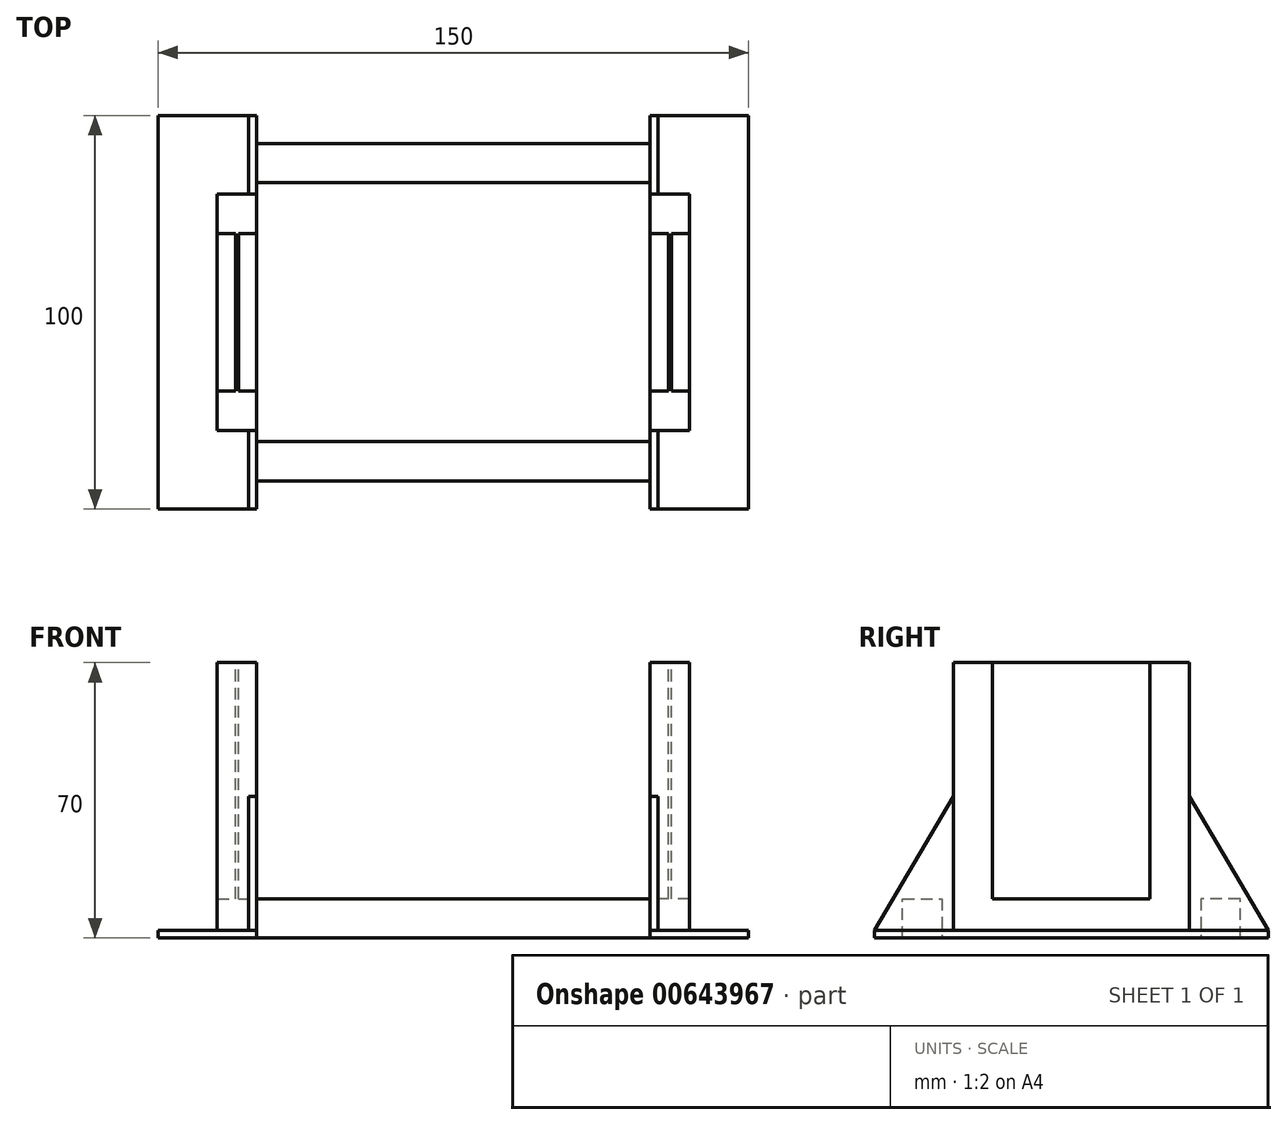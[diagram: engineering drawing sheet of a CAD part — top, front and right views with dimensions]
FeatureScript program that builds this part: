
annotation { "Feature Type Name" : "Feature", "Feature Type Description" : "" }
export const myFeature = defineFeature(function(context is Context, id is Id, definition is map)
    precondition{}
    {
        {
            var Q0;
            Q0=qCreatedBy(makeId("Right.planeOp"),FACE);
            var sketch = newSketch(context, id + "F0", { "sketchPlane" : qUnion([Q0])});
            skLineSegment(sketch, "E0", {"start": v(0, 0) * mm, "end": v(30, 0) * mm});
            skLineSegment(sketch, "E1", {"start": v(30, 0) * mm, "end": v(30, 70) * mm});
            skLineSegment(sketch, "E2", {"start": v(30, 70) * mm, "end": v(20, 70) * mm});
            skLineSegment(sketch, "E3", {"start": v(20, 70) * mm, "end": v(20, 10) * mm});
            skLineSegment(sketch, "E4", {"start": v(20, 10) * mm, "end": v(-20, 10) * mm});
            skLineSegment(sketch, "E5", {"start": v(-20, 10) * mm, "end": v(-20, 70) * mm});
            skLineSegment(sketch, "E6", {"start": v(-20, 70) * mm, "end": v(-30, 70) * mm});
            skLineSegment(sketch, "E7", {"start": v(-30, 70) * mm, "end": v(-30, 0) * mm});
            skLineSegment(sketch, "E8", {"start": v(-30, 0) * mm, "end": v(0, 0) * mm});
            skSolve(sketch);
        }
        {
            var Q0;
            Q0=makeQuery(id+"F0.imprint","IMPRINT",FACE,{"disambiguationData":[TD([[makeQuery(id+"F0.imprint","IMPRINT",EDGE,{"derivedFrom":sQuery(id+"F0.wireOp",EDGE,"E0")}),1.0]])]});
            extrude(context, id + "F1", {"entities" : qUnion([Q0]), "depth" : 10 * mm, "offsetDistance" : 25 * mm});
        }
        {
            var Q0;
            Q0=qCreatedBy(makeId("Right.planeOp"),FACE);
            cPlane(context, id + "F2", {"entities" : qUnion([Q0]), "cplaneType" : CPlaneType.OFFSET, "offset" : 5 * mm, "width" : 150 * mm, "height" : 150 * mm});
        }
        {
            var Q0;
            Q0=qCreatedBy(id+"F2.planeOp",FACE);
            var sketch = newSketch(context, id + "F3", { "sketchPlane" : qUnion([Q0])});
            skLineSegment(sketch, "E9", {"start": v(0, 0) * mm, "end": v(0, 10) * mm, "construction": true});
            skLineSegment(sketch, "E10", {"start": v(0, 10) * mm, "end": v(20, 10) * mm});
            skLineSegment(sketch, "E11", {"start": v(20, 10) * mm, "end": v(20, 70) * mm});
            skLineSegment(sketch, "E12", {"start": v(20, 70) * mm, "end": v(-20, 70) * mm});
            skLineSegment(sketch, "E13", {"start": v(-20, 70) * mm, "end": v(-20, 10) * mm});
            skLineSegment(sketch, "E14", {"start": v(-20, 10) * mm, "end": v(0, 10) * mm});
            skSolve(sketch);
        }
        {
            var Q0;
            Q0=makeQuery(id+"F3.imprint","IMPRINT",FACE,{"disambiguationData":[TD([[makeQuery(id+"F3.imprint","IMPRINT",EDGE,{"derivedFrom":sQuery(id+"F3.wireOp",EDGE,"E10")}),1.0]])]});
            extrude(context, id + "F4", {"entities" : qUnion([Q0]), "operationType" : NewBodyOperationType.ADD, "endBound" : BoundingType.SYMMETRIC, "depth" : .75 * mm, "offsetDistance" : 25 * mm});
        }
        {
            var Q0;
            Q0=makeQuery(id+"F1.opExtrude","CAP_FACE",FACE,{"disambiguationData":[OSD([sQuery(id+"F0.wireOp",EDGE,"E0"),sQuery(id+"F0.wireOp",EDGE,"E1"),sQuery(id+"F0.wireOp",EDGE,"E2"),sQuery(id+"F0.wireOp",EDGE,"E3"),sQuery(id+"F0.wireOp",EDGE,"E4"),sQuery(id+"F0.wireOp",EDGE,"E5"),sQuery(id+"F0.wireOp",EDGE,"E6"),sQuery(id+"F0.wireOp",EDGE,"E7"),sQuery(id+"F0.wireOp",EDGE,"E8")])],"isStart":true});
            var sketch = newSketch(context, id + "F5", { "sketchPlane" : qUnion([Q0])});
            skLineSegment(sketch, "E15", {"start": v(0, 0) * mm, "end": v(50, 0) * mm});
            skLineSegment(sketch, "E16", {"start": v(50, 0) * mm, "end": v(50, 2) * mm});
            skLineSegment(sketch, "E17", {"start": v(50, 2) * mm, "end": v(-50, 2) * mm});
            skLineSegment(sketch, "E18", {"start": v(-50, 2) * mm, "end": v(-50, 0) * mm});
            skLineSegment(sketch, "E19", {"start": v(-50, 0) * mm, "end": v(0, 0) * mm});
            skSolve(sketch);
        }
        {
            var Q0;
            {var subQ0=sQuery(id+"F5.wireOp",EDGE,"E17");var subQ1=makeQuery(id+"F1.opExtrude","CAP_EDGE",EDGE,{"disambiguationData":[OSD([sQuery(id+"F0.wireOp",EDGE,"E7")])],"isStart":true});var subQ2=makeQuery(id+"F5.imprint","INTERSECT",VERTEX,{"derivedFrom":[subQ1,subQ0]});Q0=makeQuery(id+"F5.imprint","IMPRINT",FACE,{"disambiguationData":[TD([[makeQuery(id+"F5.imprint","IMPRINT",EDGE,{"disambiguationData":[TD([[subQ2,-1.0]])],"derivedFrom":subQ0}),1.0]])]});}
            var Q1;
            {var subQ3=sQuery(id+"F5.wireOp",EDGE,"E16");Q1=makeQuery(id+"F5.imprint","IMPRINT",FACE,{"disambiguationData":[TD([[makeQuery(id+"F5.imprint","IMPRINT",EDGE,{"derivedFrom":subQ3}),1.0]])]});}
            var Q2;
            {var subQ0=sQuery(id+"F5.wireOp",EDGE,"E18");Q2=makeQuery(id+"F5.imprint","IMPRINT",FACE,{"disambiguationData":[TD([[makeQuery(id+"F5.imprint","IMPRINT",EDGE,{"derivedFrom":subQ0}),1.0]])]});}
            extrude(context, id + "F6", {"entities" : qUnion([Q0, Q1, Q2]), "operationType" : NewBodyOperationType.ADD, "oppositeDirection" : true, "depth" : 25 * mm, "offsetDistance" : 25 * mm});
        }
        {
            var Q0;
            Q0=makeQuery(id+"F6.boolean.opBoolean","MERGE",FACE,{"derivedFrom":[makeQuery(id+"F1.opExtrude","CAP_FACE",FACE,{"disambiguationData":[OSD([sQuery(id+"F0.wireOp",EDGE,"E0"),sQuery(id+"F0.wireOp",EDGE,"E1"),sQuery(id+"F0.wireOp",EDGE,"E2"),sQuery(id+"F0.wireOp",EDGE,"E3"),sQuery(id+"F0.wireOp",EDGE,"E4"),sQuery(id+"F0.wireOp",EDGE,"E5"),sQuery(id+"F0.wireOp",EDGE,"E6"),sQuery(id+"F0.wireOp",EDGE,"E7"),sQuery(id+"F0.wireOp",EDGE,"E8")])],"isStart":true}),makeQuery(id+"F6.opExtrude","CAP_FACE",FACE,{"disambiguationData":[OSD([sQuery(id+"F5.wireOp",EDGE,"E15"),sQuery(id+"F5.wireOp",EDGE,"E16"),sQuery(id+"F5.wireOp",EDGE,"E17"),sQuery(id+"F5.wireOp",EDGE,"E18"),sQuery(id+"F5.wireOp",EDGE,"E19")])],"isStart":true})]});
            var sketch = newSketch(context, id + "F7", { "sketchPlane" : qUnion([Q0])});
            skLineSegment(sketch, "E20", {"start": v(-30, 2) * mm, "end": v(-50, 2) * mm});
            skLineSegment(sketch, "E21", {"start": v(-50, 2) * mm, "end": v(-30, 36) * mm});
            skLineSegment(sketch, "E22", {"start": v(-30, 36) * mm, "end": v(-30, 2) * mm});
            skLineSegment(sketch, "E23.MirrorCS", {"start": v(50, 2) * mm, "end": v(30, 36) * mm});
            skLineSegment(sketch, "E24.MirrorCS", {"start": v(30, 2) * mm, "end": v(50, 2) * mm});
            skLineSegment(sketch, "E25.MirrorCS", {"start": v(30, 36) * mm, "end": v(30, 2) * mm});
            skSolve(sketch);
        }
        {
            var Q0;
            Q0=makeQuery(id+"F7.imprint","IMPRINT",FACE,{"disambiguationData":[TD([[makeQuery(id+"F7.imprint","IMPRINT",EDGE,{"derivedFrom":sQuery(id+"F7.wireOp",EDGE,"E20")}),-1.0]])]});
            var Q1;
            Q1=makeQuery(id+"F7.imprint","IMPRINT",FACE,{"disambiguationData":[TD([[makeQuery(id+"F7.imprint","IMPRINT",EDGE,{"derivedFrom":sQuery(id+"F7.wireOp",EDGE,"E23.MirrorCS")}),1.0]])]});
            extrude(context, id + "F8", {"entities" : qUnion([Q0, Q1]), "operationType" : NewBodyOperationType.ADD, "oppositeDirection" : true, "depth" : 2 * mm, "offsetDistance" : 25 * mm});
        }
        {
            var Q0;
            Q0=makeQuery(id+"F8.boolean.opBoolean","MERGE",FACE,{"derivedFrom":[makeQuery(id+"F6.boolean.opBoolean","MERGE",FACE,{"derivedFrom":[makeQuery(id+"F1.opExtrude","CAP_FACE",FACE,{"disambiguationData":[OSD([sQuery(id+"F0.wireOp",EDGE,"E0"),sQuery(id+"F0.wireOp",EDGE,"E1"),sQuery(id+"F0.wireOp",EDGE,"E2"),sQuery(id+"F0.wireOp",EDGE,"E3"),sQuery(id+"F0.wireOp",EDGE,"E4"),sQuery(id+"F0.wireOp",EDGE,"E5"),sQuery(id+"F0.wireOp",EDGE,"E6"),sQuery(id+"F0.wireOp",EDGE,"E7"),sQuery(id+"F0.wireOp",EDGE,"E8")])],"isStart":true}),makeQuery(id+"F6.opExtrude","CAP_FACE",FACE,{"disambiguationData":[OSD([sQuery(id+"F5.wireOp",EDGE,"E15"),sQuery(id+"F5.wireOp",EDGE,"E16"),sQuery(id+"F5.wireOp",EDGE,"E17"),sQuery(id+"F5.wireOp",EDGE,"E18"),sQuery(id+"F5.wireOp",EDGE,"E19")])],"isStart":true})]}),makeQuery(id+"F8.opExtrude","CAP_FACE",FACE,{"disambiguationData":[OSD([sQuery(id+"F7.wireOp",EDGE,"E20"),sQuery(id+"F7.wireOp",EDGE,"E21"),sQuery(id+"F7.wireOp",EDGE,"E22")])],"isStart":true}),makeQuery(id+"F8.opExtrude","CAP_FACE",FACE,{"disambiguationData":[OSD([sQuery(id+"F7.wireOp",EDGE,"E23.MirrorCS"),sQuery(id+"F7.wireOp",EDGE,"E24.MirrorCS"),sQuery(id+"F7.wireOp",EDGE,"E25.MirrorCS")])],"isStart":true})]});
            var sketch = newSketch(context, id + "F9", { "sketchPlane" : qUnion([Q0])});
            skLineSegment(sketch, "E26", {"start": v(-42.88, 0) * mm, "end": v(-42.88, 10) * mm});
            skLineSegment(sketch, "E27", {"start": v(-42.88, 10) * mm, "end": v(-32.88, 10) * mm});
            skLineSegment(sketch, "E28", {"start": v(-32.88, 10) * mm, "end": v(-32.88, 0) * mm});
            skLineSegment(sketch, "E29", {"start": v(-32.88, 0) * mm, "end": v(-42.88, 0) * mm});
            skLineSegment(sketch, "E30.MirrorCS", {"start": v(42.88, 10) * mm, "end": v(32.88, 10) * mm});
            skLineSegment(sketch, "E31.MirrorCS", {"start": v(32.88, 0) * mm, "end": v(42.88, 0) * mm});
            skLineSegment(sketch, "E32.MirrorCS", {"start": v(42.88, 0) * mm, "end": v(42.88, 10) * mm});
            skLineSegment(sketch, "E33.MirrorCS", {"start": v(32.88, 10) * mm, "end": v(32.88, 0) * mm});
            skSolve(sketch);
        }
        {
            var Q0;
            Q0=makeQuery(id+"F9.imprint","IMPRINT",FACE,{"disambiguationData":[TD([[makeQuery(id+"F9.imprint","IMPRINT",EDGE,{"derivedFrom":sQuery(id+"F9.wireOp",EDGE,"E26")}),-1.0]])]});
            var Q1;
            Q1=makeQuery(id+"F9.imprint","IMPRINT",FACE,{"disambiguationData":[TD([[makeQuery(id+"F9.imprint","IMPRINT",EDGE,{"derivedFrom":sQuery(id+"F9.wireOp",EDGE,"E30.MirrorCS")}),1.0]])]});
            extrude(context, id + "F10", {"entities" : qUnion([Q0, Q1]), "operationType" : NewBodyOperationType.ADD, "depth" : 50 * mm, "offsetDistance" : 25 * mm});
        }
        {
            var Q0;
            Q0=qCreatedBy(makeId("Right.planeOp"),FACE);
            cPlane(context, id + "F11", {"entities" : qUnion([Q0]), "cplaneType" : CPlaneType.OFFSET, "offset" : 50 * mm, "oppositeDirection" : true, "width" : 150 * mm, "height" : 150 * mm});
        }
        {
            var Q0;
            Q0=makeQuery(id+"F1.opExtrude","SWEPT_BODY",BODY,{"disambiguationData":[OSD([sQuery(id+"F0.wireOp",EDGE,"E0"),sQuery(id+"F0.wireOp",EDGE,"E1"),sQuery(id+"F0.wireOp",EDGE,"E2"),sQuery(id+"F0.wireOp",EDGE,"E3"),sQuery(id+"F0.wireOp",EDGE,"E4"),sQuery(id+"F0.wireOp",EDGE,"E5"),sQuery(id+"F0.wireOp",EDGE,"E6"),sQuery(id+"F0.wireOp",EDGE,"E7"),sQuery(id+"F0.wireOp",EDGE,"E8")])]});
            var Q1;
            Q1=qCreatedBy(id+"F11.planeOp",FACE);
            mirror(context, id + "F12", {"operationType" : NewBodyOperationType.ADD, "entities" : qUnion([Q0]), "mirrorPlane" : qUnion([Q1])});
        }
    });
